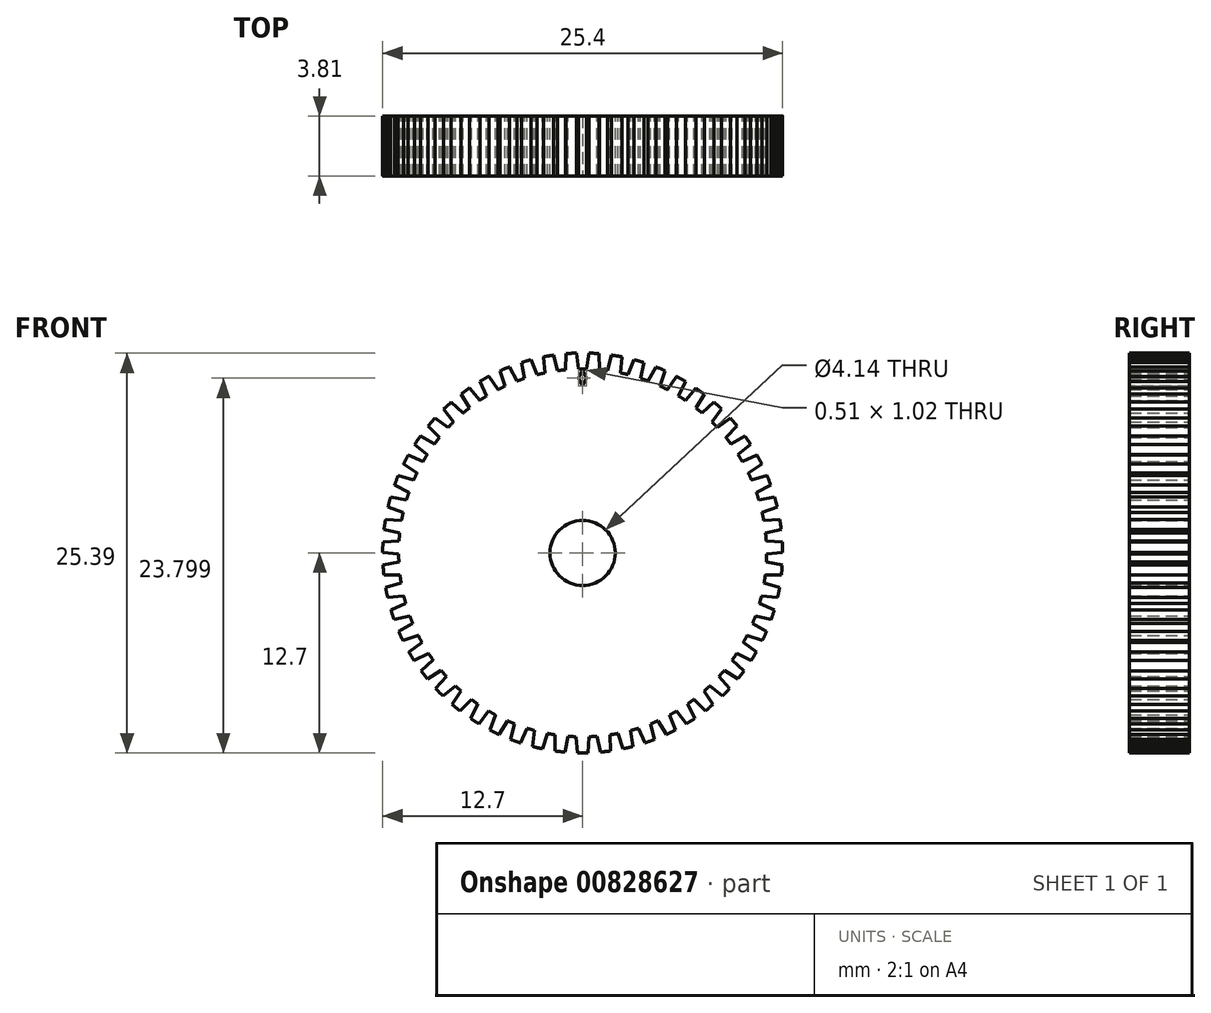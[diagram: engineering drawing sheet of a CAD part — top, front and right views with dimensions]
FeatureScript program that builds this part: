
annotation { "Feature Type Name" : "Feature", "Feature Type Description" : "" }
export const myFeature = defineFeature(function(context is Context, id is Id, definition is map)
    precondition{}
    {
        {
            var Q0;
            Q0=qCreatedBy(makeId("Front.planeOp"),FACE);
            var sketch = newSketch(context, id + "F0", { "sketchPlane" : qUnion([Q0])});
            skCircle(sketch, "E0", {"center": v(0, 0) * mm, "radius": 12.7 * mm});
            skCircle(sketch, "E1", {"center": v(0, 0) * mm, "radius": 2.07 * mm});
            skCircle(sketch, "E2", {"center": v(0, 0) * mm, "radius": 11.68 * mm});
            skLineSegment(sketch, "E3", {"start": v(-0.25, 11.68) * mm, "end": v(-0.4, 12.7) * mm});
            skLineSegment(sketch, "E4.MirrorCS", {"start": v(0.25, 11.68) * mm, "end": v(0.4, 12.7) * mm});
            skSolve(sketch);
        }
        {
            var Q0;
            Q0=makeQuery(id+"F0.imprint","IMPRINT",FACE,{"disambiguationData":[TD([[makeQuery(id+"F0.imprint","IMPRINT",EDGE,{"derivedFrom":sQuery(id+"F0.wireOp",EDGE,"E1")}),-1.0]])]});
            var Q1;
            {var subQ0=sQuery(id+"F0.wireOp",EDGE,"E3");Q1=makeQuery(id+"F0.imprint","IMPRINT",FACE,{"disambiguationData":[TD([[makeQuery(id+"F0.imprint","IMPRINT",EDGE,{"derivedFrom":subQ0}),1.0]])]});}
            extrude(context, id + "F1", {"entities" : qUnion([Q0, Q1]), "depth" : 3.8 * mm, "offsetDistance" : 25.4 * mm});
        }
        {
            var Q0;
            Q0=makeQuery(id+"F1.opExtrude","SWEPT_FACE",FACE,{"disambiguationData":[OSD([sQuery(id+"F0.wireOp",EDGE,"E3")])]});
            var Q1;
            Q1=makeQuery(id+"F1.opExtrude","SWEPT_FACE",FACE,{"disambiguationData":[OSD([sQuery(id+"F0.wireOp",EDGE,"E2")])]});
            var Q2;
            Q2=makeQuery(id+"F1.opExtrude","SWEPT_FACE",FACE,{"disambiguationData":[OSD([sQuery(id+"F0.wireOp",EDGE,"E4.MirrorCS")])]});
            var Q3;
            Q3=makeQuery(id+"F1.opExtrude","SWEPT_FACE",FACE,{"disambiguationData":[OSD([sQuery(id+"F0.wireOp",EDGE,"E2")])]});
            circularPattern(context, id + "F2", {"patternType" : PatternType.FACE, "faces" : qUnion([Q0, Q1, Q2]), "axis" : qUnion([Q3]), "angle" : 360 * degree, "instanceCount" : 55, "equalSpace" : true});
        }
        {
            var Q0;
            Q0=qCreatedBy(makeId("Front.planeOp"),FACE);
            var sketch = newSketch(context, id + "F3", { "sketchPlane" : qUnion([Q0])});
            skLineSegment(sketch, "E5", {"start": v(0, 11.6) * mm, "end": v(0, 10.6) * mm});
            skLineSegment(sketch, "E6", {"start": v(0, 10.6) * mm, "end": v(-0.25, 11.1) * mm});
            skPoint(sketch, "E6.endSnap0", {"position": v(0, 11.1) * mm});
            skLineSegment(sketch, "E7", {"start": v(0, 11.6) * mm, "end": v(-0.25, 11.1) * mm});
            skLineSegment(sketch, "E8.MirrorCS", {"start": v(0, 11.6) * mm, "end": v(0.25, 11.1) * mm});
            skLineSegment(sketch, "E9.MirrorCS", {"start": v(0, 10.6) * mm, "end": v(0.25, 11.1) * mm});
            skSolve(sketch);
        }
        {
            var Q0;
            Q0 = qSketchRegion(id + "F3", true);
            extrude(context, id + "F4", {"entities" : qUnion([Q0]), "operationType" : NewBodyOperationType.REMOVE, "endBound" : BoundingType.SYMMETRIC, "oppositeDirection" : true, "depth" : 25.4 * mm, "offsetDistance" : 25.4 * mm});
        }
    });
